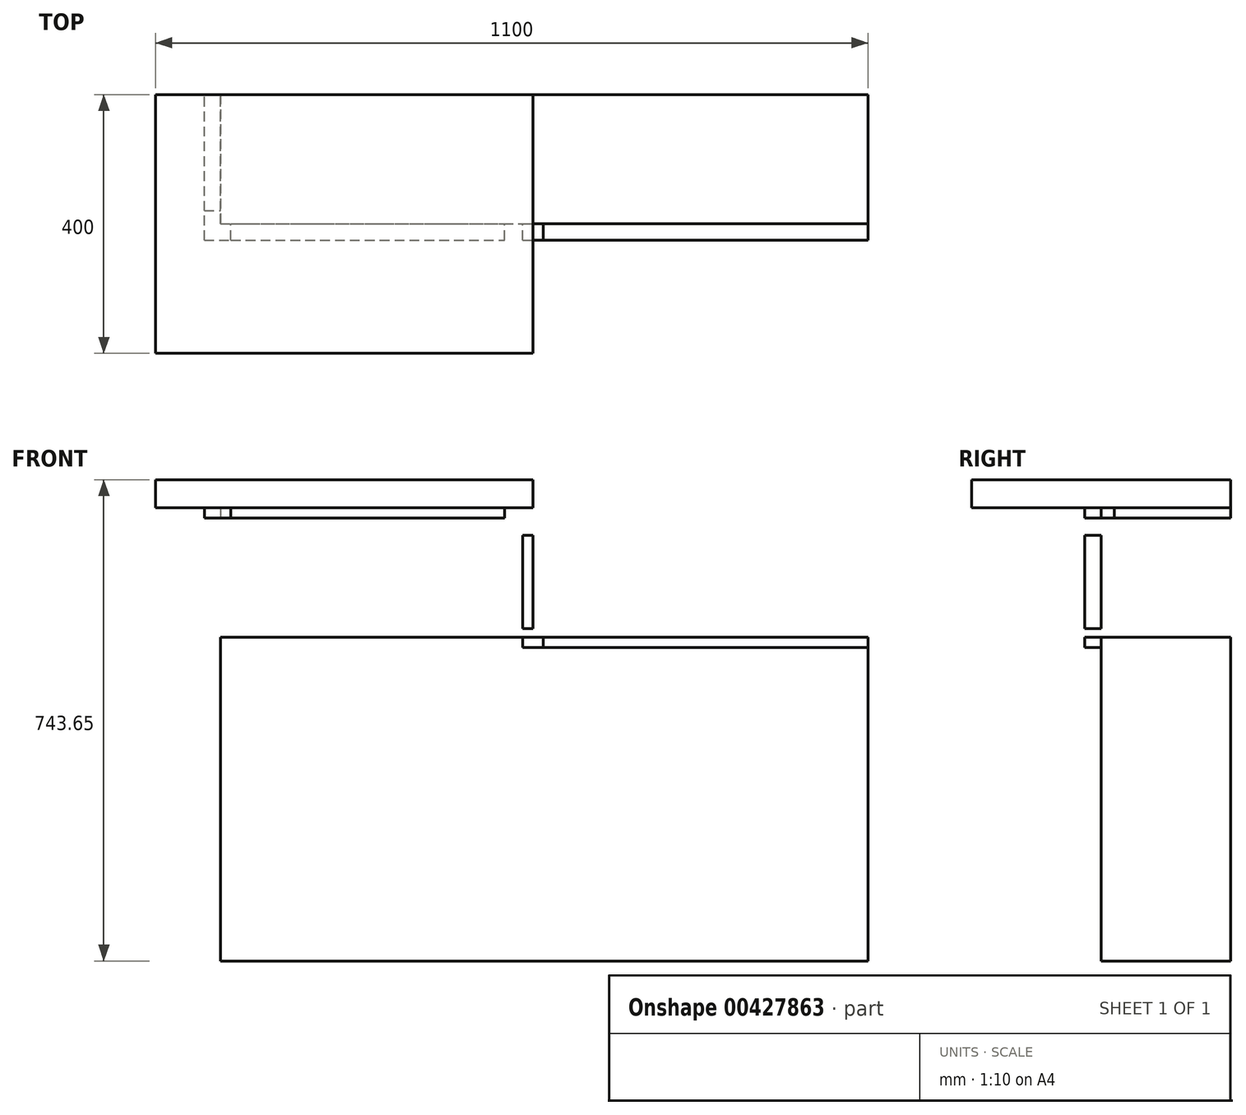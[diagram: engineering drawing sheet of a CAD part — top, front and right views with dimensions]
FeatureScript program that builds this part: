
annotation { "Feature Type Name" : "Feature", "Feature Type Description" : "" }
export const myFeature = defineFeature(function(context is Context, id is Id, definition is map)
    precondition{}
    {
        {
            var Q0;
            Q0=qCreatedBy(makeId("Front.planeOp"),FACE);
            var sketch = newSketch(context, id + "F0", { "sketchPlane" : qUnion([Q0])});
            skLineSegment(sketch, "E0.bottom", {"start": v(-675.65, 248.36) * mm, "end": v(324.35, 248.36) * mm});
            skLineSegment(sketch, "E0.top", {"start": v(-675.65, -251.64) * mm, "end": v(324.35, -251.64) * mm});
            skLineSegment(sketch, "E0.left", {"start": v(-675.65, 248.36) * mm, "end": v(-675.65, -251.64) * mm});
            skLineSegment(sketch, "E0.right", {"start": v(324.35, 248.36) * mm, "end": v(324.35, -251.64) * mm});
            skLineSegment(sketch, "E1.bottom", {"start": v(-675.65, 248.36) * mm, "end": v(-192.78, 248.36) * mm});
            skLineSegment(sketch, "E1.top", {"start": v(-675.65, 448.36) * mm, "end": v(-192.78, 448.36) * mm});
            skLineSegment(sketch, "E1.left", {"start": v(-675.65, 248.36) * mm, "end": v(-675.65, 448.36) * mm});
            skLineSegment(sketch, "E1.right", {"start": v(-192.78, 248.36) * mm, "end": v(-192.78, 448.36) * mm});
            skLineSegment(sketch, "E2.bottom", {"start": v(324.35, 248.36) * mm, "end": v(-192.78, 248.36) * mm});
            skLineSegment(sketch, "E2.top", {"start": v(324.35, 492.01) * mm, "end": v(-192.78, 492.01) * mm});
            skLineSegment(sketch, "E2.left", {"start": v(324.35, 248.36) * mm, "end": v(324.35, 492.01) * mm});
            skLineSegment(sketch, "E2.right", {"start": v(-192.78, 248.36) * mm, "end": v(-192.78, 492.01) * mm});
            skLineSegment(sketch, "E3.bottom", {"start": v(-192.78, 492.01) * mm, "end": v(-675.65, 492.01) * mm});
            skLineSegment(sketch, "E3.top", {"start": v(-192.78, 448.36) * mm, "end": v(-675.65, 448.36) * mm});
            skLineSegment(sketch, "E3.left", {"start": v(-192.78, 492.01) * mm, "end": v(-192.78, 448.36) * mm});
            skLineSegment(sketch, "E3.right", {"start": v(-675.65, 492.01) * mm, "end": v(-675.65, 448.36) * mm});
            skSolve(sketch);
        }
        {
            var Q0;
            Q0=makeQuery(id+"F0.imprint","IMPRINT",FACE,{"disambiguationData":[TD([[makeQuery(id+"F0.imprint","IMPRINT",EDGE,{"derivedFrom":sQuery(id+"F0.wireOp",EDGE,"E0.top")}),1.0]])]});
            var Q1;
            Q1=makeQuery(id+"F0.imprint","IMPRINT",FACE,{"disambiguationData":[TD([[makeQuery(id+"F0.imprint","IMPRINT",EDGE,{"derivedFrom":sQuery(id+"F0.wireOp",EDGE,"E1.bottom")}),1.0]])]});
            extrude(context, id + "F1", {"entities" : qUnion([Q0, Q1]), "oppositeDirection" : true, "depth" : 200 * mm, "offsetDistance" : 25 * mm});
        }
        {
            var Q0;
            Q0=makeQuery(id+"F0.imprint","IMPRINT",FACE,{"disambiguationData":[TD([[makeQuery(id+"F0.imprint","IMPRINT",EDGE,{"derivedFrom":sQuery(id+"F0.wireOp",EDGE,"E3.bottom")}),1.0]])]});
            var Q1;
            Q1=makeQuery(id+"F0.imprint","IMPRINT",FACE,{"disambiguationData":[TD([[makeQuery(id+"F0.imprint","IMPRINT",EDGE,{"derivedFrom":sQuery(id+"F0.wireOp",EDGE,"E2.bottom")}),-1.0]])]});
            extrude(context, id + "F2", {"entities" : qUnion([Q0, Q1]), "operationType" : NewBodyOperationType.ADD, "depth" : 200 * mm, "offsetDistance" : 25 * mm, "hasSecondDirection" : true, "secondDirectionOppositeDirection" : true, "secondDirectionDepth" : 200 * mm});
        }
        {
            var Q0;
            Q0=makeQuery(id+"F1.opExtrude","CAP_FACE",FACE,{"disambiguationData":[OSD([sQuery(id+"F0.wireOp",EDGE,"E0.top"),sQuery(id+"F0.wireOp",EDGE,"E0.left"),sQuery(id+"F0.wireOp",EDGE,"E0.right"),sQuery(id+"F0.wireOp",EDGE,"E1.left"),sQuery(id+"F0.wireOp",EDGE,"E2.bottom"),sQuery(id+"F0.wireOp",EDGE,"E2.right"),sQuery(id+"F0.wireOp",EDGE,"E3.top")])],"isStart":true});
            var sketch = newSketch(context, id + "F3", { "sketchPlane" : qUnion([Q0])});
            skLineSegment(sketch, "E4.bottom", {"start": v(-675.65, 448.36) * mm, "end": v(-192.78, 448.36) * mm});
            skLineSegment(sketch, "E4.top", {"start": v(-675.65, 432.36) * mm, "end": v(-208.78, 432.36) * mm});
            skLineSegment(sketch, "E4.left", {"start": v(-675.65, 448.36) * mm, "end": v(-675.65, 432.36) * mm});
            skLineSegment(sketch, "E4.right", {"start": v(-192.78, 448.36) * mm, "end": v(-192.78, 432.36) * mm});
            skPoint(sketch, "E5.oppositeSnap0", {"position": v(-192.78, 348.36) * mm});
            skLineSegment(sketch, "E5.top", {"start": v(-208.78, 232.36) * mm, "end": v(-192.78, 232.36) * mm});
            skLineSegment(sketch, "E5.left", {"start": v(-208.78, 432.36) * mm, "end": v(-208.78, 232.36) * mm});
            skLineSegment(sketch, "E5.right", {"start": v(-192.78, 423.36) * mm, "end": v(-192.78, 248.36) * mm});
            skLineSegment(sketch, "E6.bottom", {"start": v(-192.78, 232.36) * mm, "end": v(324.35, 232.36) * mm});
            skLineSegment(sketch, "E6.top", {"start": v(-192.78, 248.36) * mm, "end": v(324.35, 248.36) * mm});
            skLineSegment(sketch, "E6.right", {"start": v(324.35, 232.36) * mm, "end": v(324.35, 248.36) * mm});
            skLineSegment(sketch, "E7", {"start": v(-176.99, 248.36) * mm, "end": v(-176.99, 232.36) * mm});
            skLineSegment(sketch, "E8", {"start": v(-192.78, 262.01) * mm, "end": v(-208.78, 262.01) * mm});
            skLineSegment(sketch, "E9", {"start": v(-236.85, 432.36) * mm, "end": v(-236.85, 448.36) * mm});
            skLineSegment(sketch, "E10", {"start": v(-208.78, 405.83) * mm, "end": v(-192.78, 405.83) * mm});
            skLineSegment(sketch, "E11", {"start": v(-659.65, 448.36) * mm, "end": v(-659.65, 432.36) * mm});
            skSolve(sketch);
        }
        {
            var Q0;
            {var subQ0=sQuery(id+"F3.wireOp",EDGE,"E6.right");Q0=makeQuery(id+"F3.imprint","IMPRINT",FACE,{"disambiguationData":[TD([[makeQuery(id+"F3.imprint","IMPRINT",EDGE,{"derivedFrom":subQ0}),-1.0]])]});}
            var Q1;
            {var subQ0=sQuery(id+"F3.wireOp",EDGE,"E9");Q1=makeQuery(id+"F3.imprint","IMPRINT",FACE,{"disambiguationData":[TD([[makeQuery(id+"F3.imprint","IMPRINT",EDGE,{"derivedFrom":subQ0}),1.0]])]});}
            var Q2;
            {var subQ0=sQuery(id+"F3.wireOp",EDGE,"E8");Q2=makeQuery(id+"F3.imprint","IMPRINT",FACE,{"disambiguationData":[TD([[makeQuery(id+"F3.imprint","IMPRINT",EDGE,{"derivedFrom":subQ0}),-1.0]])]});}
            extrude(context, id + "F4", {"entities" : qUnion([Q0, Q1, Q2]), "depth" : 25 * mm, "offsetDistance" : 25 * mm});
        }
        {
            var Q0;
            {var subQ0=sQuery(id+"F3.wireOp",EDGE,"E4.left");Q0=makeQuery(id+"F3.imprint","IMPRINT",FACE,{"disambiguationData":[TD([[makeQuery(id+"F3.imprint","IMPRINT",EDGE,{"derivedFrom":subQ0}),1.0]])]});}
            var Q1;
            {var subQ4=sQuery(id+"F3.wireOp",EDGE,"E4.right");Q1=makeQuery(id+"F3.imprint","IMPRINT",FACE,{"disambiguationData":[TD([[makeQuery(id+"F3.imprint","IMPRINT",EDGE,{"derivedFrom":subQ4}),1.0]])]});}
            var Q2;
            {var subQ1=sQuery(id+"F3.wireOp",EDGE,"E5.top");Q2=makeQuery(id+"F3.imprint","IMPRINT",FACE,{"disambiguationData":[TD([[makeQuery(id+"F3.imprint","IMPRINT",EDGE,{"derivedFrom":subQ1}),1.0]])]});}
            extrude(context, id + "F5", {"entities" : qUnion([Q0, Q1, Q2]), "depth" : 25 * mm, "offsetDistance" : 25 * mm});
        }
        {
            var Q0;
            Q0=makeQuery(id+"F2.boolean.opBoolean","MERGE",FACE,{"derivedFrom":[makeQuery(id+"F1.opExtrude","SWEPT_FACE",FACE,{"disambiguationData":[OSD([sQuery(id+"F0.wireOp",EDGE,"E0.left"),sQuery(id+"F0.wireOp",EDGE,"E1.left")])]}),makeQuery(id+"F2.opExtrude","SWEPT_FACE",FACE,{"disambiguationData":[OSD([sQuery(id+"F0.wireOp",EDGE,"E3.right")])]})]});
            var sketch = newSketch(context, id + "F6", { "sketchPlane" : qUnion([Q0])});
            skLineSegment(sketch, "E12.bottom", {"start": v(200, 448.36) * mm, "end": v(-200, 448.36) * mm});
            skLineSegment(sketch, "E12.top", {"start": v(200, 492.01) * mm, "end": v(-200, 492.01) * mm});
            skLineSegment(sketch, "E12.left", {"start": v(200, 448.36) * mm, "end": v(200, 492.01) * mm});
            skLineSegment(sketch, "E12.right", {"start": v(-200, 448.36) * mm, "end": v(-200, 492.01) * mm});
            skSolve(sketch);
        }
        {
            var Q0;
            Q0 = qSketchRegion(id + "F6", true);
            extrude(context, id + "F7", {"entities" : qUnion([Q0]), "operationType" : NewBodyOperationType.ADD, "depth" : 100 * mm, "offsetDistance" : 25 * mm});
        }
        {
            var Q0;
            Q0=makeQuery(id+"F2.boolean.opBoolean","MERGE",FACE,{"derivedFrom":[makeQuery(id+"F1.opExtrude","SWEPT_FACE",FACE,{"disambiguationData":[OSD([sQuery(id+"F0.wireOp",EDGE,"E0.left"),sQuery(id+"F0.wireOp",EDGE,"E1.left")])]}),makeQuery(id+"F2.opExtrude","SWEPT_FACE",FACE,{"disambiguationData":[OSD([sQuery(id+"F0.wireOp",EDGE,"E3.right")])]})]});
            var sketch = newSketch(context, id + "F8", { "sketchPlane" : qUnion([Q0])});
            skLineSegment(sketch, "E13.bottom", {"start": v(0, 448.36) * mm, "end": v(-200, 448.36) * mm});
            skLineSegment(sketch, "E13.top", {"start": v(0, 432.36) * mm, "end": v(-200, 432.36) * mm});
            skLineSegment(sketch, "E13.left", {"start": v(0, 448.36) * mm, "end": v(0, 432.36) * mm});
            skLineSegment(sketch, "E13.right", {"start": v(-200, 448.36) * mm, "end": v(-200, 432.36) * mm});
            skLineSegment(sketch, "E14", {"start": v(-20.39, 432.36) * mm, "end": v(-20.39, 448.36) * mm});
            skSolve(sketch);
        }
        {
            var Q0;
            {var subQ0=sQuery(id+"F8.wireOp",EDGE,"E13.left");Q0=makeQuery(id+"F8.imprint","IMPRINT",FACE,{"disambiguationData":[TD([[makeQuery(id+"F8.imprint","IMPRINT",EDGE,{"derivedFrom":subQ0}),-1.0]])]});}
            var Q1;
            Q1=makeQuery(id+"F5.opExtrude","SWEPT_FACE",FACE,{"disambiguationData":[OSD([sQuery(id+"F3.wireOp",EDGE,"E4.left")])]});
            extrude(context, id + "F9", {"entities" : qUnion([Q0, Q1]), "operationType" : NewBodyOperationType.ADD, "depth" : 25 * mm, "offsetDistance" : 25 * mm});
        }
        {
            var Q0;
            {var subQ0=sQuery(id+"F8.wireOp",EDGE,"E13.right");Q0=makeQuery(id+"F8.imprint","IMPRINT",FACE,{"disambiguationData":[TD([[makeQuery(id+"F8.imprint","IMPRINT",EDGE,{"derivedFrom":subQ0}),1.0]])]});}
            extrude(context, id + "F10", {"entities" : qUnion([Q0]), "depth" : 25 * mm, "offsetDistance" : 25 * mm});
        }
    });
